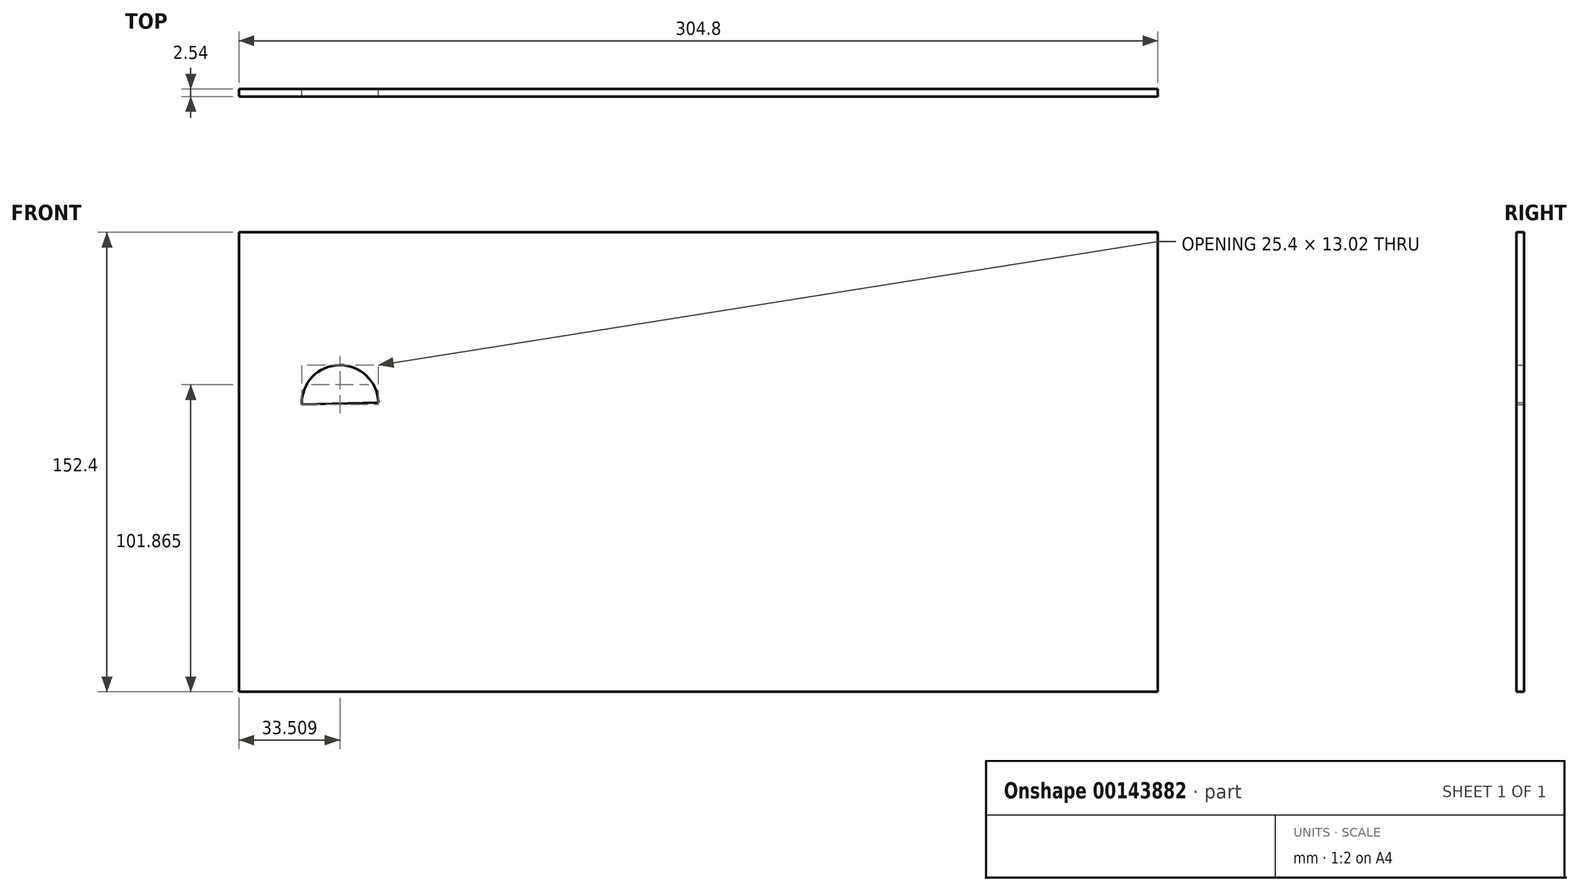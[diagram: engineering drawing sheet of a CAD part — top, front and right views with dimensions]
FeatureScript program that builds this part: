
annotation { "Feature Type Name" : "Feature", "Feature Type Description" : "" }
export const myFeature = defineFeature(function(context is Context, id is Id, definition is map)
    precondition{}
    {
        {
            var Q0;
            Q0=qCreatedBy(makeId("Front.planeOp"),FACE);
            var sketch = newSketch(context, id + "F0", { "sketchPlane" : qUnion([Q0])});
            skLineSegment(sketch, "E0.bottom", {"start": v(152.4, -76.2) * mm, "end": v(-152.4, -76.2) * mm});
            skLineSegment(sketch, "E0.top", {"start": v(152.4, 76.2) * mm, "end": v(-152.4, 76.2) * mm});
            skLineSegment(sketch, "E0.left", {"start": v(152.4, -76.2) * mm, "end": v(152.4, 76.2) * mm});
            skLineSegment(sketch, "E0.right", {"start": v(-152.4, -76.2) * mm, "end": v(-152.4, 76.2) * mm});
            skPoint(sketch, "E0.middle", {"position": v(0, 0) * mm});
            skArc(sketch, "E1", {"start": v(-106.2, 19.79) * mm, "mid": v(-119.2, 32.17) * mm, "end": v(-131.6, 19.16) * mm});
            skLineSegment(sketch, "E2", {"start": v(-131.6, 19.16) * mm, "end": v(-106.2, 19.79) * mm});
            skSolve(sketch);
        }
        {
            var Q0;
            Q0=makeQuery(id+"F0.imprint","IMPRINT",FACE,{"disambiguationData":[TD([[makeQuery(id+"F0.imprint","IMPRINT",EDGE,{"derivedFrom":sQuery(id+"F0.wireOp",EDGE,"E0.bottom")}),-1.0]])]});
            extrude(context, id + "F1", {"entities" : qUnion([Q0]), "depth" : 2.54 * mm});
        }
    });
